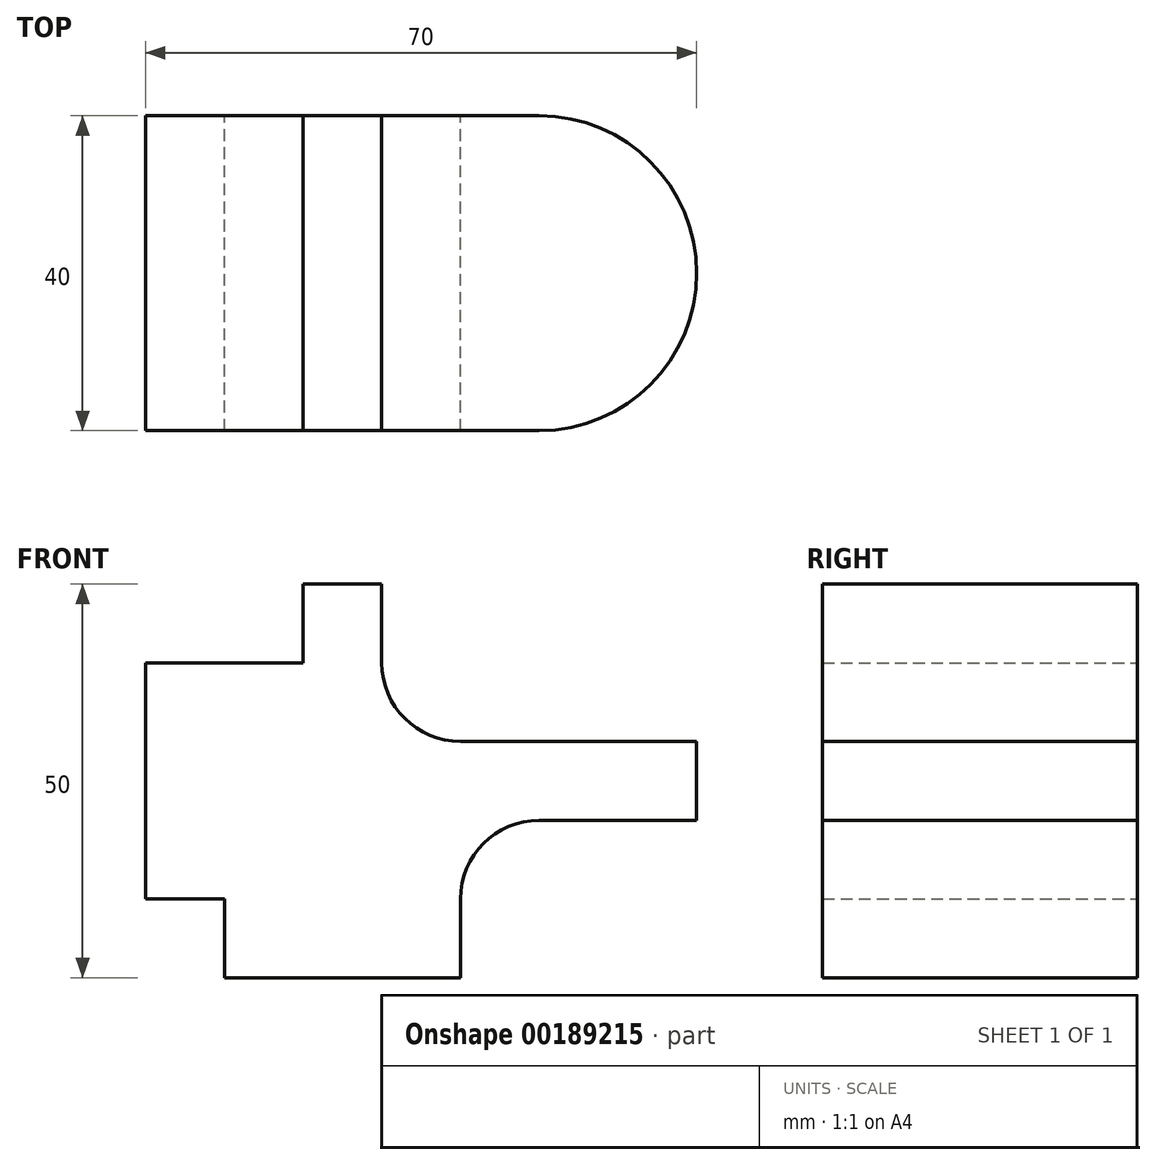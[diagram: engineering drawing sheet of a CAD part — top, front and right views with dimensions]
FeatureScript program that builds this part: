
annotation { "Feature Type Name" : "Feature", "Feature Type Description" : "" }
export const myFeature = defineFeature(function(context is Context, id is Id, definition is map)
    precondition{}
    {
        {
            var Q0;
            Q0=qCreatedBy(makeId("Front.planeOp"),FACE);
            var sketch = newSketch(context, id + "F0", { "sketchPlane" : qUnion([Q0])});
            skLineSegment(sketch, "E0", {"start": v(0, 0) * mm, "end": v(0, 30) * mm});
            skLineSegment(sketch, "E1", {"start": v(0, 30) * mm, "end": v(20, 30) * mm});
            skLineSegment(sketch, "E2", {"start": v(20, 30) * mm, "end": v(20, 40) * mm});
            skLineSegment(sketch, "E3", {"start": v(20, 40) * mm, "end": v(30, 40) * mm});
            skLineSegment(sketch, "E4", {"start": v(30, 40) * mm, "end": v(30, 30) * mm});
            skLineSegment(sketch, "E5", {"start": v(40, 20) * mm, "end": v(70, 20) * mm});
            skLineSegment(sketch, "E6", {"start": v(70, 20) * mm, "end": v(70, 10) * mm});
            skLineSegment(sketch, "E7", {"start": v(70, 10) * mm, "end": v(50, 10) * mm});
            skLineSegment(sketch, "E8", {"start": v(40, 0) * mm, "end": v(40, -10) * mm});
            skLineSegment(sketch, "E9", {"start": v(40, -10) * mm, "end": v(10, -10) * mm});
            skLineSegment(sketch, "E10", {"start": v(10, -10) * mm, "end": v(10, 0) * mm});
            skLineSegment(sketch, "E11", {"start": v(10, 0) * mm, "end": v(0, 0) * mm});
            skPoint(sketch, "E12.visualSharp", {"position": v(30, 20) * mm});
            skArc(sketch, "E12.filletArc", {"start": v(30, 30) * mm, "mid": v(32.93, 22.93) * mm, "end": v(40, 20) * mm});
            skPoint(sketch, "E13.visualSharp", {"position": v(40, 10) * mm});
            skArc(sketch, "E13.filletArc", {"start": v(50, 10) * mm, "mid": v(42.93, 7.07) * mm, "end": v(40, 0) * mm});
            skSolve(sketch);
        }
        {
            var Q0;
            Q0=makeQuery(id+"F0.imprint","IMPRINT",FACE,{"disambiguationData":[TD([[makeQuery(id+"F0.imprint","IMPRINT",EDGE,{"derivedFrom":sQuery(id+"F0.wireOp",EDGE,"E0")}),-1.0]])]});
            extrude(context, id + "F1", {"entities" : qUnion([Q0]), "endBound" : BoundingType.SYMMETRIC, "depth" : 40 * mm});
        }
        {
            var Q0;
            Q0=makeQuery(id+"F1.opExtrude","CAP_EDGE",EDGE,{"disambiguationData":[OSD([sQuery(id+"F0.wireOp",EDGE,"E6")])],"isStart":false});
            var Q1;
            Q1=makeQuery(id+"F1.opExtrude","CAP_EDGE",EDGE,{"disambiguationData":[OSD([sQuery(id+"F0.wireOp",EDGE,"E6")])],"isStart":true});
            fillet(context, id + "F2", {"entities" : qUnion([Q0, Q1]), "radius" : 20 * mm, "tangentPropagation" : true, "allowEdgeOverflow" : false});
        }
    });
